# Revit family: Skystar_SK-MB_14-4tr-MD600_RFA2019
name_source: partatom
category: Mechanical Equipment
units: mm (PartAtom-declared; Revit-internal decimal feet)

## family parameters
Always vertical = Yes
Cut with Voids When Loaded = Yes
OmniClass Number = 23.75.00.00
OmniClass Title = Climate Control (HVAC)
Part Type = Normal
Room Calculation Point = Yes
Round Connector Dimension = Use Diameter
Shared = Yes
Work Plane-Based = Yes

## types (6) — shared parameters
4Tubi = Yes
A = 572 mm  [stored 1.87664 ft]
D_QC_IN = 15 mm  [stored 0.0492126 ft]
D_Q_C_OUT = 15 mm  [stored 0.0492126 ft]
Default Elevation = 1219 mm
Description = Kazetový fancoil
Foro controsoffitto = 582 mm
Lato macchina = 572 mm  [stored 1.87664 ft]
Lookup Table Name = SABIANA-SkyStar
Manufacturer = Hydronix
S = 348 mm
THIN_def = 70 °C
Type Comments = Výměník čtyřtrubkový; motor asynchronní 3-otáčkový; MB-RTU komunikační karta; čelní deska plech lakovaný barva bílá RAL 9003
Type Image = md-600.jpg
URL = www.hydronix.cz
cpa = 1.0050 J/(g·°C)
cph = 4.1860 J/(g·°C)
rho_a = 1.2000 kg/m³
rho_h = 1000.2970 kg/m³
zero-valued in all types: BVc, COBie_Cost, COBie_ExpectedLife, COBie_ReplacementCost, COBie_WarrantyDurationLabour, COBie_WarrantyDurationParts

## per-type parameters (varying)
| type | Assembly Code | Filtro elettrostatico | Taglia |
| SK-MB 04 MD | SK-MB 04 (o.č.: 0079180)+MD600 (o.č.: 9079420) | Yes | 4 |
| SK-MB 14 MD | SK-MB 14 (o.č.: 0079181)+MD600 (o.č.: 9079420) | No | 14 |
| SK-MB 34 MD | SK-MB 34 (o.č.: 0079183)+MD600 (o.č.: 9079420) | No | 34 |
| SK-MB 24 MD | SK-MB 24 (o.č.: 0079182)+MD600 (o.č.: 9079420) | No | 24 |
| SK-MB 26 MD | SK-MB 26 (o.č.: 0079187)+MD600 (o.č.: 9079420) | No | 26 |
| SK-MB 36 MD | SK-MB 36 (o.č.: 0079188)+MD600 (o.č.: 9079420) | No | 36 |

note: column(s) folded — value = type name in every type: Model

note: [stored X ft] marks values corroborated as IEEE doubles in the binary element streams (Revit-internal decimal feet)

## geometry (parser evidence)
native form markers: Blend x4
no freeform markers — native parametric forms only
